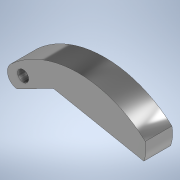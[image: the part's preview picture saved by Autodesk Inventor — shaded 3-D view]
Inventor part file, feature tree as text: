
AUTODESK INVENTOR PART (.ipt)
format: ipt  version: 2021 (Build 250183000, 183)  size: 114,176 bytes
history: native  units: mm
features: extrude x2, sketch x2, other x1
ambient origin geometry x8: Origin, YZ Plane, XZ Plane, XY Plane, X Axis, Y Axis, Z Axis, Center Point
bodies: Body1 (feature_tree)
feature tree (5):
  other  "Sólido1"
  extrude  "Extrusão1"  Depth=6.04mm
  extrude  "Extrusão2"  Depth=1.2mm
  sketch  "Esboço2"  dims[d8=9.0mm d9=6.04mm]
  sketch  "Esboço3"  dims[d10=0.8mm d11=0.843mm d12=1.2mm d13=0.0mm d14=0.5mm d16=2.472987mm d17=3.141005mm d18=0.0mm d19=0.0mm]
